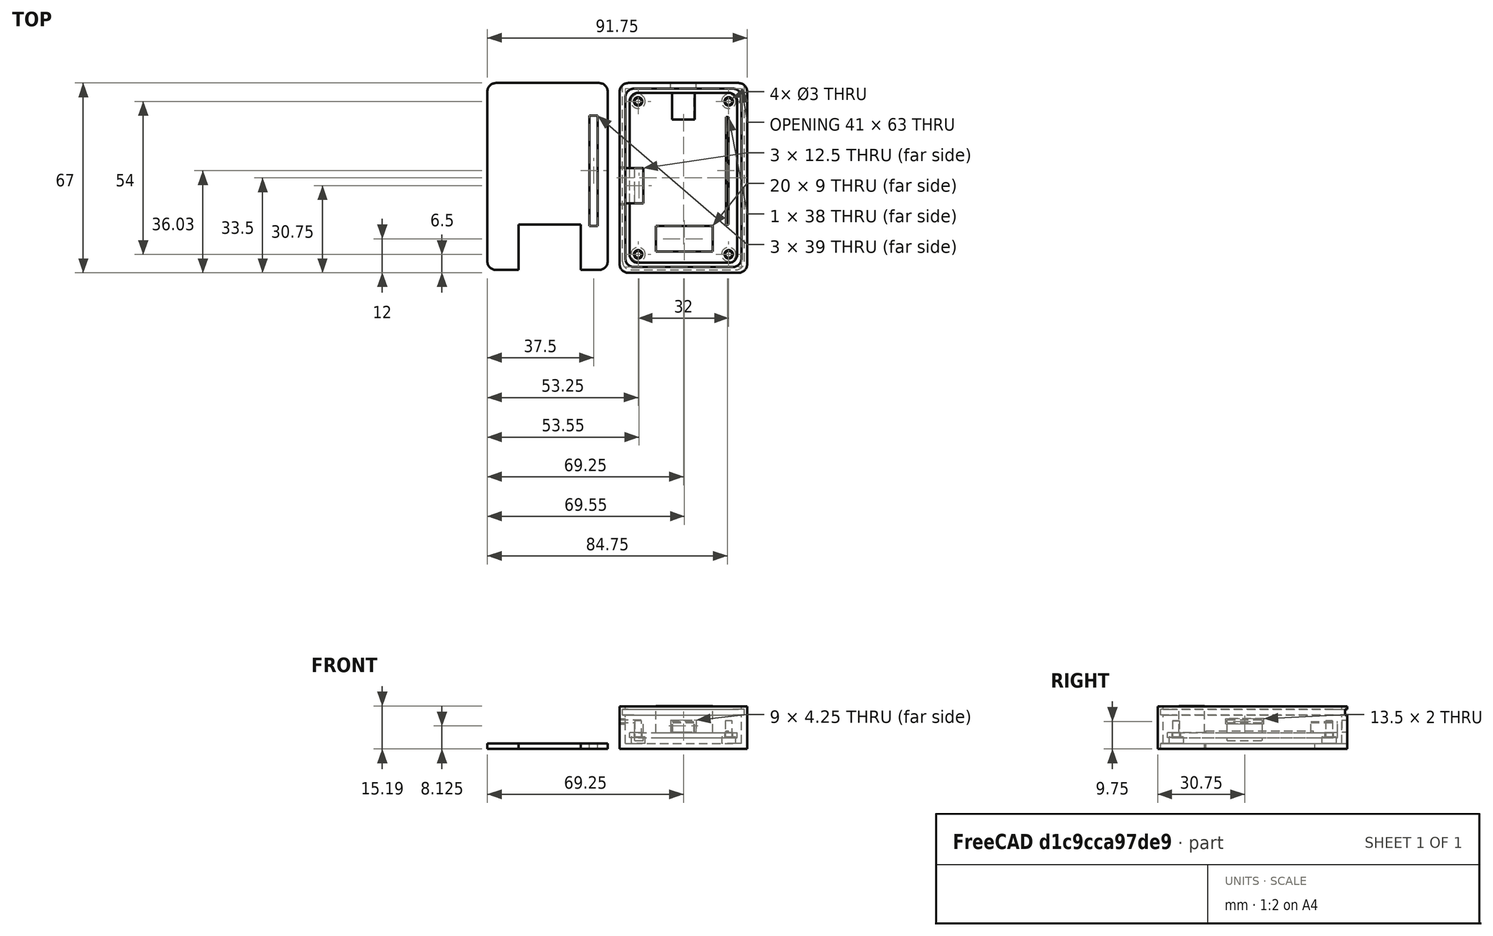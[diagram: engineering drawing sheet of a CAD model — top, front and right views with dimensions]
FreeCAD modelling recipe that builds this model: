
FCSTD DOCUMENT  (FreeCAD 0.21R33668 +26 (Git))
Label: busPiratev3
License: All rights reserved
LicenseURL: https://en.wikipedia.org/wiki/All_rights_reserved
objects: Part::Box×15, Part::Cylinder×12, Part::Cut×12, Part::Fillet×11, Part::MultiFuse×5
note: 55 computed .brp shape members not serialized (recipe doc carries the construction recipe); baked Part::Feature solids carry a one-line shape summary decoded from their .brp

FEATURE [Part::Box] Box  label="Placa"
  AttacherType = Attacher::AttachEngine3D
  Height = 1.8
  Length = 38
  Width = 60
FEATURE [Part::Box] Box001  label="Conector"
  AttacherType = Attacher::AttachEngine3D
  Height = 11.19
  Length = 20
  Placement = pos=(9.3,4,0) rot=(0,0,1;0rad)
  Width = 9
FEATURE [Part::MultiFuse] Fusion
  Shapes = -> [Box001,Box]
FEATURE [Part::Cylinder] Cylinder  label="hueco de tornillo 1"
  Angle = 360
  AttacherType = Attacher::AttachEngine3D
  FirstAngle = 0
  Height = 10
  Placement = pos=(3,3,0) rot=(0,0,1;0rad)
  Radius = 1.5
  SecondAngle = 0
FEATURE [Part::Cylinder] Cylinder001  label="hueco de tornillo 002"
  Angle = 360
  AttacherType = Attacher::AttachEngine3D
  FirstAngle = 0
  Height = 10
  Placement = pos=(35,3,0) rot=(0,0,1;0rad)
  Radius = 1.5
  SecondAngle = 0
FEATURE [Part::Cylinder] Cylinder002  label="hueco de tornillo 003"
  Angle = 360
  AttacherType = Attacher::AttachEngine3D
  FirstAngle = 0
  Height = 10
  Placement = pos=(3,57,0) rot=(0,0,1;0rad)
  Radius = 1.5
  SecondAngle = 0
FEATURE [Part::Cylinder] Cylinder003  label="hueco de tornillo 004"
  Angle = 360
  AttacherType = Attacher::AttachEngine3D
  FirstAngle = 0
  Height = 10
  Placement = pos=(35,57,0) rot=(0,0,1;0rad)
  Radius = 1.5
  SecondAngle = 0
FEATURE [Part::Cut] Cut
  Base = -> Fusion
  Tool = -> Cylinder002
FEATURE [Part::Cut] Cut001
  Base = -> Cut
  Tool = -> Cylinder
FEATURE [Part::Cut] Cut002
  Base = -> Cut001
  Tool = -> Cylinder003
FEATURE [Part::Cut] Cut003
  Base = -> Cut002
  Tool = -> Cylinder001
FEATURE [Part::Fillet] Fillet
  Base = -> Cut003
  Edges = 1 edges r=3: [Edge13]
FEATURE [Part::Fillet] Fillet001
  Base = -> Fillet
  Edges = 1 edges r=3: [Edge22]
FEATURE [Part::Fillet] Fillet002
  Base = -> Fillet001
  Edges = 1 edges r=3: [Edge23]
FEATURE [Part::Fillet] Fillet003
  Base = -> Fillet002
  Edges = 1 edges r=3: [Edge23]
FEATURE [Part::Box] Box002  label="Cubo"
  AttacherType = Attacher::AttachEngine3D
  Height = 7.3
  Length = 8.3
  Placement = pos=(-3.5,21,-1) rot=(0,0,1;0rad)
  Width = 12.5
FEATURE [Part::Box] Box003  label="Cubo001"
  AttacherType = Attacher::AttachEngine3D
  Height = 6.3
  Length = 5.3
  Placement = pos=(-3.5,21,-1) rot=(0,0,1;0rad)
  Width = 12.5
FEATURE [Part::Cut] Cut004  label="Conector001"
  Base = -> Box002
  Tool = -> Box003
FEATURE [Part::MultiFuse] Fusion001
  Shapes = -> [Fillet003,Cut004]
FEATURE [Part::Box] Box004  label="Cubo002"
  AttacherType = Attacher::AttachEngine3D
  Height = 5.7
  Length = 8
  Placement = pos=(15,50.6,0) rot=(0,0,1;0rad)
  Width = 9.4
FEATURE [Part::Box] Box005  label="Cubo003"
  AttacherType = Attacher::AttachEngine3D
  Height = 3.5
  Length = 7.6
  Placement = pos=(15.2,50.6,1.8) rot=(0,0,1;0rad)
  Width = 9.4
FEATURE [Part::Cut] Cut005
  Base = -> Box004
  Tool = -> Box005
FEATURE [Part::MultiFuse] Fusion002
  Shapes = -> [Fusion001,Cut005]
FEATURE [Part::Box] Box006  label="Leds"
  AttacherType = Attacher::AttachEngine3D
  Height = 2.4
  Length = 1
  Placement = pos=(34,13.53,0) rot=(0,0,1;0rad)
  Width = 38
FEATURE [Part::MultiFuse] Fusion003
  Placement = pos=(3.5,3.5,4) rot=(0,0,1;0rad)
  Shapes = -> [Fusion002,Box006]
FEATURE [Part::Box] Box007  label="Cubo004"
  AttacherType = Attacher::AttachEngine3D
  Height = 15
  Length = 45
  Width = 67
FEATURE [Part::Box] Box008  label="Cubo005"
  AttacherType = Attacher::AttachEngine3D
  Height = 13
  Length = 41
  Placement = pos=(2,2,2) rot=(0,0,1;0rad)
  Width = 63
FEATURE [Part::Cut] Cut006
  Base = -> Box007
  Tool = -> Box008
FEATURE [Part::Cylinder] Cylinder004  label="Cilindro"
  Angle = 360
  AttacherType = Attacher::AttachEngine3D
  FirstAngle = 0
  Height = 10
  Placement = pos=(6.5,6.5,0) rot=(0,0,1;0rad)
  Radius = 1.2
  SecondAngle = 0
FEATURE [Part::Cylinder] Cylinder005  label="Cilindro001"
  Angle = 360
  AttacherType = Attacher::AttachEngine3D
  FirstAngle = 0
  Height = 10
  Placement = pos=(38.5,6.5,0) rot=(0,0,1;0rad)
  Radius = 1.2
  SecondAngle = 0
FEATURE [Part::Cylinder] Cylinder006  label="Cilindro002"
  Angle = 360
  AttacherType = Attacher::AttachEngine3D
  FirstAngle = 0
  Height = 10
  Placement = pos=(6.5,60.5,0) rot=(0,0,1;0rad)
  Radius = 1.2
  SecondAngle = 0
FEATURE [Part::Cylinder] Cylinder007  label="Cilindro003"
  Angle = 360
  AttacherType = Attacher::AttachEngine3D
  FirstAngle = 0
  Height = 10
  Placement = pos=(38.5,60.5,0) rot=(0,0,1;0rad)
  Radius = 1.2
  SecondAngle = 0
FEATURE [Part::Cylinder] Cylinder008  label="Cilindro004"
  Angle = 360
  AttacherType = Attacher::AttachEngine3D
  FirstAngle = 0
  Height = 3.3
  Placement = pos=(38.5,60.5,1) rot=(0,0,1;0rad)
  Radius = 2.5
  SecondAngle = 0
FEATURE [Part::Cylinder] Cylinder009  label="Cilindro005"
  Angle = 360
  AttacherType = Attacher::AttachEngine3D
  FirstAngle = 0
  Height = 3.3
  Placement = pos=(6.5,60.5,1) rot=(0,0,1;0rad)
  Radius = 2.5
  SecondAngle = 0
FEATURE [Part::Cylinder] Cylinder010  label="Cilindro006"
  Angle = 360
  AttacherType = Attacher::AttachEngine3D
  FirstAngle = 0
  Height = 3.3
  Placement = pos=(6.5,6.5,1) rot=(0,0,1;0rad)
  Radius = 2.5
  SecondAngle = 0
FEATURE [Part::Cylinder] Cylinder011  label="Cilindro007"
  Angle = 360
  AttacherType = Attacher::AttachEngine3D
  FirstAngle = 0
  Height = 3.3
  Placement = pos=(38.5,6.5,1) rot=(0,0,1;0rad)
  Radius = 2.5
  SecondAngle = 0
FEATURE [Part::Fillet] Fillet004
  Base = -> Cut006
  Edges = 1 edges r=3: [Edge6]
FEATURE [Part::Fillet] Fillet005
  Base = -> Fillet004
  Edges = 1 edges r=3: [Edge24]
FEATURE [Part::Fillet] Fillet006
  Base = -> Fillet005
  Edges = 6 edges r=3: [Edge12,Edge16,Edge19,Edge22,Edge26,Edge29]
FEATURE [Part::Box] Box009  label="Cubo006"
  AttacherType = Attacher::AttachEngine3D
  Height = 2
  Length = 43
  Placement = pos=(1,0,21) rot=(0,0,1;0rad)
  Width = 70
FEATURE [Part::Fillet] Fillet007
  Base = -> Box009
  Edges = 3 edges r=3: [Edge1,Edge5,Edge7]
FEATURE [Part::Fillet] Fillet008
  Base = -> Fillet007
  Edges = 1 edges r=3: [Edge4]
  Placement = pos=(0,1,-9) rot=(0,0,1;0rad)
FEATURE [Part::Box] Box010  label="Cubo007"
  AttacherType = Attacher::AttachEngine3D
  Height = 2
  Length = 42.5
  Placement = pos=(1,1,21) rot=(0,0,1;0rad)
  Width = 66
FEATURE [Part::Fillet] Fillet009
  Base = -> Box010
  Edges = 3 edges r=3: [Edge1,Edge5,Edge7]
FEATURE [Part::Fillet] Fillet010
  Base = -> Fillet009
  Edges = 1 edges r=3: [Edge4]
  Placement = pos=(0,0,-10) rot=(0,0,1;0rad)
FEATURE [Part::Box] Box011  label="Cubo008"
  AttacherType = Attacher::AttachEngine3D
  Height = 3
  Length = 22
  Placement = pos=(12,0,10.5) rot=(0,0,1;0rad)
  Width = 17
FEATURE [Part::Cut] Cut007
  Base = -> Fillet010
  Tool = -> Box011
FEATURE [Part::Box] Box012  label="Leds001"
  AttacherType = Attacher::AttachEngine3D
  Height = 3.4
  Length = 3
  Placement = pos=(37,16.53,10) rot=(0,0,1;0rad)
  Width = 39
FEATURE [Part::Cut] Cut008
  Base = -> Cut007
  Placement = pos=(-47.75,0,-11) rot=(0,0,1;0rad)
  Tool = -> Box012
FEATURE [Part::Box] Box013  label="Cubo009"
  AttacherType = Attacher::AttachEngine3D
  Height = 2
  Length = 4
  Placement = pos=(0,24,8.75) rot=(0,0,1;0rad)
  Width = 13.5
FEATURE [Part::Cut] Cut009
  Base = -> Fillet006
  Tool = -> Box013
FEATURE [Part::Box] Box014  label="Cubo010"
  AttacherType = Attacher::AttachEngine3D
  Height = 4.25
  Length = 9
  Placement = pos=(18,59,6) rot=(0,0,1;0rad)
  Width = 10
FEATURE [Part::Cut] Cut010
  Base = -> Cut009
  Tool = -> Box014
FEATURE [Part::MultiFuse] Fusion004
  Shapes = -> [Cut010,Cylinder008,Cylinder007,Cylinder011,Cylinder005,Cylinder010,Cylinder004,Cylinder006,Cylinder009]
FEATURE [Part::Cut] Cut011
  Base = -> Fusion004
  Tool = -> Fillet008
